FCSTD DOCUMENT  (FreeCAD 0.22R35720 (Git))
Label: polar test v3 
License: All rights reserved
LicenseURL: https://en.wikipedia.org/wiki/All_rights_reserved
objects: TechDraw::DrawViewDimension×8, TechDraw::DrawViewBalloon×7, Sketcher::SketchObject×1, TechDraw::DrawSVGTemplate×1, TechDraw::DrawViewPart×1, TechDraw::DrawPage×1
note: 17 computed .brp shape members not serialized (recipe doc carries the construction recipe); baked Part::Feature solids carry a one-line shape summary decoded from their .brp

FEATURE [Sketcher::SketchObject] Sketch
  FullyConstrained = false
  sketch-geometry (41):
    g0: LineSegment StartX=46.4714 StartY=19.2491 StartZ=0 EndX=19.2491 EndY=46.4714 EndZ=0
    g1: LineSegment StartX=19.2491 StartY=46.4714 StartZ=0 EndX=-19.2491 EndY=46.4714 EndZ=0
    g2: LineSegment StartX=-19.2491 StartY=46.4714 StartZ=0 EndX=-46.4714 EndY=19.2491 EndZ=0
    g3: LineSegment StartX=-46.4714 StartY=19.2491 StartZ=0 EndX=-46.4714 EndY=-19.2491 EndZ=0
    g4: LineSegment StartX=-46.4714 StartY=-19.2491 StartZ=0 EndX=-19.2491 EndY=-46.4714 EndZ=0
    g5: LineSegment StartX=-19.2491 StartY=-46.4714 StartZ=0 EndX=19.2491 EndY=-46.4714 EndZ=0
    g6: LineSegment StartX=19.2491 StartY=-46.4714 StartZ=0 EndX=46.4714 EndY=-19.2491 EndZ=0
    g7: LineSegment StartX=46.4714 StartY=-19.2491 StartZ=0 EndX=46.4714 EndY=19.2491 EndZ=0
    g8: Circle CenterX=0 CenterY=0 CenterZ=0 NormalX=0 NormalY=0 NormalZ=1 AngleXU=0 Radius=50.3003
    g9: LineSegment StartX=79.9038 StartY=0 StartZ=0 EndX=56.5005 EndY=56.5005 EndZ=0
    g10: LineSegment StartX=56.5005 StartY=56.5005 StartZ=0 EndX=0 EndY=79.9038 EndZ=0
    g11: LineSegment StartX=-1.9e-15 StartY=79.9038 StartZ=0 EndX=-56.5005 EndY=56.5005 EndZ=0
    g12: LineSegment StartX=-56.5005 StartY=56.5005 StartZ=0 EndX=-79.9038 EndY=7.1e-15 EndZ=0
    g13: LineSegment StartX=-79.9038 StartY=3.8e-15 StartZ=0 EndX=-56.5005 EndY=-56.5005 EndZ=0
    g14: LineSegment StartX=-56.5005 StartY=-56.5005 StartZ=0 EndX=0 EndY=-79.9038 EndZ=0
    g15: LineSegment StartX=-1.9e-15 StartY=-79.9038 StartZ=0 EndX=56.5005 EndY=-56.5005 EndZ=0
    g16: LineSegment StartX=56.5005 StartY=-56.5005 StartZ=0 EndX=79.9038 EndY=0 EndZ=0
    g17: Circle CenterX=0 CenterY=0 CenterZ=0 NormalX=0 NormalY=0 NormalZ=1 AngleXU=0 Radius=79.9038
    g18: ArcOfCircle CenterX=-19.2491 CenterY=46.4714 CenterZ=0 NormalX=0 NormalY=0 NormalZ=1 AngleXU=0 Radius=8 StartAngle=1.04839 EndAngle=2.8786
    g19: ArcOfCircle CenterX=46.4714 CenterY=-19.2491 CenterZ=0 NormalX=0 NormalY=0 NormalZ=1 AngleXU=0 Radius=8 StartAngle=4.97538 EndAngle=6.80559
    g20: ArcOfCircle CenterX=19.2491 CenterY=-46.4714 CenterZ=0 NormalX=0 NormalY=0 NormalZ=1 AngleXU=0 Radius=8 StartAngle=4.18998 EndAngle=6.02019
    g21: ArcOfCircle CenterX=-19.2491 CenterY=-46.4714 CenterZ=0 NormalX=0 NormalY=0 NormalZ=1 AngleXU=0 Radius=8 StartAngle=3.40458 EndAngle=5.2348
    g22: ArcOfCircle CenterX=-46.4714 CenterY=-19.2491 CenterZ=0 NormalX=0 NormalY=0 NormalZ=1 AngleXU=0 Radius=8 StartAngle=2.61919 EndAngle=4.4494
    g23: ArcOfCircle CenterX=-46.4714 CenterY=19.2491 CenterZ=0 NormalX=0 NormalY=0 NormalZ=1 AngleXU=0 Radius=8 StartAngle=1.83379 EndAngle=3.664
    g24: ArcOfCircle CenterX=-1.9e-15 CenterY=-79.9038 CenterZ=0 NormalX=0 NormalY=0 NormalZ=1 AngleXU=0 Radius=30.5779 StartAngle=1.04839 EndAngle=2.0932
    g25: ArcOfCircle CenterX=-56.5005 CenterY=-56.5005 CenterZ=0 NormalX=0 NormalY=0 NormalZ=1 AngleXU=0 Radius=30.5779 StartAngle=0.262991 EndAngle=1.3078
    g26: ArcOfCircle CenterX=-79.9038 CenterY=3.8e-15 CenterZ=0 NormalX=0 NormalY=0 NormalZ=1 AngleXU=0 Radius=30.5779 StartAngle=5.76078 EndAngle=6.80559
    g27: ArcOfCircle CenterX=-56.5005 CenterY=56.5005 CenterZ=0 NormalX=0 NormalY=0 NormalZ=1 AngleXU=0 Radius=30.5779 StartAngle=4.97538 EndAngle=6.02019
    g28: ArcOfCircle CenterX=-1.9e-15 CenterY=79.9038 CenterZ=0 NormalX=0 NormalY=0 NormalZ=1 AngleXU=0 Radius=30.5779 StartAngle=4.18998 EndAngle=5.2348
    g29: ArcOfCircle CenterX=56.5005 CenterY=-56.5005 CenterZ=0 NormalX=0 NormalY=0 NormalZ=1 AngleXU=0 Radius=30.5779 StartAngle=1.83379 EndAngle=2.8786
    g30: ArcOfCircle CenterX=79.9038 CenterY=3.8e-15 CenterZ=0 NormalX=0 NormalY=0 NormalZ=1 AngleXU=0 Radius=30.5779 StartAngle=2.61919 EndAngle=3.664
    g31: ArcOfCircle CenterX=56.5005 CenterY=56.5005 CenterZ=0 NormalX=0 NormalY=0 NormalZ=1 AngleXU=0 Radius=30.5779 StartAngle=3.40458 EndAngle=4.4494
    g32: ArcOfCircle CenterX=19.2491 CenterY=46.4714 CenterZ=0 NormalX=0 NormalY=0 NormalZ=1 AngleXU=0 Radius=8 StartAngle=0.262991 EndAngle=2.0932
    g33: ArcOfCircle CenterX=46.4714 CenterY=19.2491 CenterZ=0 NormalX=0 NormalY=0 NormalZ=1 AngleXU=0 Radius=8 StartAngle=5.76078 EndAngle=7.59099
    g34: ArcOfCircle CenterX=-79.9038 CenterY=1.276e-13 CenterZ=0 NormalX=0 NormalY=0 NormalZ=1 AngleXU=0 Radius=30.5779 StartAngle=5.76078 EndAngle=6.80559
    g35: ArcOfCircle CenterX=-56.5005 CenterY=-56.5005 CenterZ=0 NormalX=0 NormalY=0 NormalZ=1 AngleXU=0 Radius=30.5779 StartAngle=0.262991 EndAngle=1.30781
    g36: ArcOfCircle CenterX=5.889e-13 CenterY=79.9038 CenterZ=0 NormalX=0 NormalY=0 NormalZ=1 AngleXU=0 Radius=30.5779 StartAngle=4.18998 EndAngle=5.2348
    g37: ArcOfCircle CenterX=-56.5005 CenterY=56.5005 CenterZ=0 NormalX=0 NormalY=0 NormalZ=1 AngleXU=0 Radius=30.5779 StartAngle=4.97538 EndAngle=6.02019
    g38: ArcOfCircle CenterX=-79.9038 CenterY=1.612e-13 CenterZ=0 NormalX=0 NormalY=0 NormalZ=1 AngleXU=0 Radius=30.5779 StartAngle=5.76078 EndAngle=6.80559
    g39: LineSegment StartX=0 StartY=0 StartZ=0 EndX=0 EndY=54.8429 EndZ=0
    g40: LineSegment StartX=0 StartY=0 StartZ=0 EndX=56.3585 EndY=0 EndZ=0
  constraints (85):
    c: Coincident(g0,g1)
    c: Coincident(g1,g2)
    c: Coincident(g2,g3)
    c: Coincident(g3,g4)
    c: Coincident(g4,g5)
    c: Coincident(g5,g6)
    c: Coincident(g6,g7)
    c: Coincident(g7,g0)
    c: Equal(g0, g1-g7) x7
    c: PointOnObject(g0,g8)
    c: PointOnObject(g1,g8)
    c: PointOnObject(g2,g8)
    c: PointOnObject(g3,g8)
    c: PointOnObject(g4,g8)
    c: PointOnObject(g5,g8)
    c: PointOnObject(g6,g8)
    c: PointOnObject(g7,g8)
    c: Coincident(g8,g-1)
    c: Coincident(g9,g10)
    c: Coincident(g10,g11)
    c: Coincident(g11,g12)
    c: Coincident(g12,g13)
    c: Coincident(g13,g14)
    c: Coincident(g14,g15)
    c: Coincident(g15,g16)
    c: Coincident(g16,g9)
    c: Equal(g9, g10-g16) x7
    c: PointOnObject(g9,g17)
    c: PointOnObject(g11,g17)
    c: PointOnObject(g12,g17)
    c: PointOnObject(g13,g17)
    c: PointOnObject(g14,g17)
    c: PointOnObject(g15,g17)
    c: PointOnObject(g16,g17)
    c: Coincident(g17,g8)
    c: PointOnObject(g16,g-1)
    c: Coincident(g18,g1)
    c: Coincident(g19,g6)
    c: Coincident(g20,g5)
    c: Coincident(g21,g4)
    c: Coincident(g22,g3)
    c: Coincident(g23,g2)
    c: Equal(g19,g20)
    c: Equal(g20,g21)
    c: Equal(g21,g22)
    c: Equal(g22,g23)
    c: Coincident(g24,g14)
    c: Coincident(g25,g13)
    c: Coincident(g26,g12)
    c: Coincident(g27,g11)
    c: Coincident(g28,g10)
    c: Equal(g24,g25)
    c: Equal(g25,g26)
    c: Equal(g26,g27)
    c: Radius(g18) = 8
    c: Coincident(g32,g31)
    c: PointOnObject(g32,g28)
    c: Coincident(g33,g31)
    c: Coincident(g33,g30)
    c: Coincident(g19,g30)
    c: Coincident(g19,g29)
    c: Coincident(g23,g27)
    c: Coincident(g23,g26)
    c: PointOnObject(g34,g23)
    c: PointOnObject(g34,g22)
    c: PointOnObject(g35,g22)
    c: Coincident(g22,g26)
    c: Coincident(g22,g25)
    c: Coincident(g21,g25)
    c: Coincident(g21,g24)
    c: Coincident(g20,g24)
    c: Coincident(g20,g29)
    c: Tangent(g18,g28) = 1.5708
    c: Coincident(g18,g27)
    c: PointOnObject(g35,g21)
    c: PointOnObject(g37,g18)
    c: PointOnObject(g36,g18)
    c: PointOnObject(g36,g32)
    c: PointOnObject(g38,g23)
    c: PointOnObject(g37,g23)
    c: PointOnObject(g38,g22)
    c: Coincident(g39,g8)
    c: PointOnObject(g39,g-2)
    c: Coincident(g40,g39)
    c: PointOnObject(g40,g-1)
FEATURE [TechDraw::DrawSVGTemplate] Template
  EditableTexts = Designed_by_Name=Stephen; Drawing_number=T10001; FC-Date=24 Jan 24; FC-SC=NTS; FC-SH=1; FC-Title=Polar Cordinate Test; Subtitle=Test dims for G-Code; Weight=NA
  Height = 210
  Orientation = 1
  Template = F:/Program Files/FreeCAD/data/Mod/TechDraw/Templates/A4_LandscapeTD.svg
  Width = 297
FEATURE [TechDraw::DrawViewPart] View
  CoarseView = false
  Direction = (0,0,1)
  Focus = 100
  HardHidden = false
  IsoCount = 0
  IsoHidden = false
  IsoVisible = false
  LockPosition = false
  Perspective = false
  Rotation = 0
  ScaleType = 0
  ScrubCount = 0
  SeamHidden = false
  SeamVisible = false
  SmoothHidden = false
  SmoothVisible = true
  Source = -> [Sketch]
  X = 82.6714
  XDirection = (1,0,0)
  Y = 102.876
FEATURE [TechDraw::DrawViewDimension] Dimension
  AngleOverride = false
  Arbitrary = false
  ArbitraryTolerances = false
  EqualTolerance = true
  ExtensionAngle = 0
  FormatSpec = C%.3w
  FormatSpecOverTolerance = %+.2w
  FormatSpecUnderTolerance = %+.2w
  Inverted = false
  LineAngle = 0
  LockPosition = false
  MeasureType = 1
  OverTolerance = 0
  References2D = -> [View]
  Rotation = 0
  ScaleType = 0
  TheoreticalExact = false
  Type = 1
  UnderTolerance = 0
  X = 6.68518
  Y = 61.6572
FEATURE [TechDraw::DrawViewDimension] Dimension001
  AngleOverride = false
  Arbitrary = false
  ArbitraryTolerances = false
  EqualTolerance = true
  ExtensionAngle = 0
  FormatSpec = C%.3w
  FormatSpecOverTolerance = %+.2w
  FormatSpecUnderTolerance = %+.2w
  Inverted = false
  LineAngle = 0
  LockPosition = false
  MeasureType = 1
  OverTolerance = 0
  References2D = -> [View]
  Rotation = 0
  ScaleType = 0
  TheoreticalExact = false
  Type = 1
  UnderTolerance = 0
  X = 12.5435
  Y = 68.6572
FEATURE [TechDraw::DrawViewDimension] Dimension002
  AngleOverride = false
  Arbitrary = false
  ArbitraryTolerances = false
  EqualTolerance = true
  ExtensionAngle = 0
  FormatSpec = C%.3w
  FormatSpecOverTolerance = %+.2w
  FormatSpecUnderTolerance = %+.2w
  Inverted = false
  LineAngle = 0
  LockPosition = false
  MeasureType = 1
  OverTolerance = 0
  References2D = -> [View]
  Rotation = 0
  ScaleType = 0
  TheoreticalExact = false
  Type = 1
  UnderTolerance = 0
  X = 23.3321
  Y = 75.6572
FEATURE [TechDraw::DrawViewDimension] Dimension003
  AngleOverride = false
  Arbitrary = false
  ArbitraryTolerances = false
  EqualTolerance = true
  ExtensionAngle = 0
  FormatSpec = C%.3w
  FormatSpecOverTolerance = %+.2w
  FormatSpecUnderTolerance = %+.2w
  Inverted = false
  LineAngle = 0
  LockPosition = false
  MeasureType = 1
  OverTolerance = 0
  References2D = -> [View]
  Rotation = 0
  ScaleType = 0
  TheoreticalExact = false
  Type = 1
  UnderTolerance = 0
  X = 25.7587
  Y = 82.6572
FEATURE [TechDraw::DrawViewDimension] Dimension004
  AngleOverride = false
  Arbitrary = false
  ArbitraryTolerances = false
  EqualTolerance = true
  ExtensionAngle = 0
  FormatSpec = %.3w X30.514
  FormatSpecOverTolerance = %+.2w
  FormatSpecUnderTolerance = %+.2w
  Inverted = false
  LineAngle = 0
  LockPosition = false
  MeasureType = 1
  OverTolerance = 0
  References2D = -> [View]
  Rotation = 0
  ScaleType = 0
  TheoreticalExact = false
  Type = 2
  UnderTolerance = 0
  X = 62.415
  Y = 2.33371
FEATURE [TechDraw::DrawViewDimension] Dimension005
  AngleOverride = false
  Arbitrary = false
  ArbitraryTolerances = false
  EqualTolerance = true
  ExtensionAngle = 0
  FormatSpec = %.3w X53.948
  FormatSpecOverTolerance = %+.2w
  FormatSpecUnderTolerance = %+.2w
  Inverted = false
  LineAngle = 0
  LockPosition = false
  MeasureType = 1
  OverTolerance = 0
  References2D = -> [View]
  Rotation = 0
  ScaleType = 0
  TheoreticalExact = false
  Type = 2
  UnderTolerance = 0
  X = 71.0076
  Y = 2.52937
FEATURE [TechDraw::DrawViewDimension] Dimension006
  AngleOverride = false
  Arbitrary = false
  ArbitraryTolerances = false
  EqualTolerance = true
  ExtensionAngle = 0
  FormatSpec = %.3w X97.102
  FormatSpecOverTolerance = %+.2w
  FormatSpecUnderTolerance = %+.2w
  Inverted = false
  LineAngle = 0
  LockPosition = false
  MeasureType = 1
  OverTolerance = 0
  References2D = -> [View]
  Rotation = 0
  ScaleType = 0
  TheoreticalExact = false
  Type = 2
  UnderTolerance = 0
  X = 78.5385
  Y = 1.81564
FEATURE [TechDraw::DrawViewDimension] Dimension007
  AngleOverride = false
  Arbitrary = false
  ArbitraryTolerances = false
  EqualTolerance = true
  ExtensionAngle = 0
  FormatSpec = %.3w X106.808
  FormatSpecOverTolerance = %+.2w
  FormatSpecUnderTolerance = %+.2w
  Inverted = false
  LineAngle = 0
  LockPosition = false
  MeasureType = 1
  OverTolerance = 0
  References2D = -> [View]
  Rotation = 0
  ScaleType = 0
  TheoreticalExact = false
  Type = 2
  UnderTolerance = 0
  X = 86.0693
  Y = 2.82657
FEATURE [TechDraw::DrawViewBalloon] Balloon001
  BubbleShape = 0
  EndType = 0
  EndTypeScale = 1
  KinkLength = 5
  LockPosition = false
  OriginX = 91.633
  OriginY = -0.0634794
  Rotation = 0
  ScaleType = 0
  ShapeScale = 0.8
  SourceView = -> View
  Text = C
  TextWrapLen = -1
  X = 107.917
  Y = -13.6856
FEATURE [TechDraw::DrawViewBalloon] Balloon002
  BubbleShape = 0
  EndType = 0
  EndTypeScale = 1
  KinkLength = 5
  LockPosition = false
  OriginX = -1.27035
  OriginY = 54.7937
  Rotation = 0
  ScaleType = 0
  ShapeScale = 0.8
  SourceView = -> View
  Text = X
  TextWrapLen = -1
  X = -22.6787
  Y = 64.7071
FEATURE [TechDraw::DrawViewBalloon] Balloon
  BubbleShape = 6
  EndType = 0
  EndTypeScale = 1
  KinkLength = 5
  LockPosition = false
  OriginX = 14.3139
  OriginY = 53.2187
  Rotation = 0
  ScaleType = 0
  ShapeScale = 0.8
  SourceView = -> View
  Text = N502
  TextWrapLen = -1
  X = 6.17742
  Y = 37.8269
FEATURE [TechDraw::DrawViewBalloon] Balloon003
  BubbleShape = 6
  EndType = 0
  EndTypeScale = 1
  KinkLength = 5
  LockPosition = false
  OriginX = 26.8661
  OriginY = 48.9541
  Rotation = 0
  ScaleType = 0
  ShapeScale = 0.8
  SourceView = -> View
  Text = N503
  TextWrapLen = -1
  X = 11.2974
  Y = 28.0766
FEATURE [TechDraw::DrawViewBalloon] Balloon004
  BubbleShape = 6
  EndType = 0
  EndTypeScale = 1
  KinkLength = 5
  LockPosition = false
  OriginX = 47.6077
  OriginY = 26.7883
  Rotation = 0
  ScaleType = 0
  ShapeScale = 0.8
  SourceView = -> View
  Text = N504
  TextWrapLen = -1
  X = 26.9072
  Y = 19.0058
FEATURE [TechDraw::DrawViewBalloon] Balloon005
  BubbleShape = 6
  EndType = 0
  EndTypeScale = 1
  KinkLength = 5
  LockPosition = false
  OriginX = 52.879
  OriginY = 15.3319
  Rotation = 0
  ScaleType = 0
  ShapeScale = 0.8
  SourceView = -> View
  Text = N505
  TextWrapLen = -1
  X = 34.302
  Y = 7.54941
FEATURE [TechDraw::DrawViewBalloon] Balloon006
  BubbleShape = 6
  EndType = 0
  EndTypeScale = 1
  KinkLength = 5
  LockPosition = false
  OriginX = -16.2009
  OriginY = 53.2187
  Rotation = 0
  ScaleType = 0
  ShapeScale = 0.8
  SourceView = -> View
  Text = N501
  TextWrapLen = -1
  X = -12.1272
  Y = 32.1642
FEATURE [TechDraw::DrawPage] Page
  KeepUpdated = true
  NextBalloonIndex = 19
  ProjectionType = 0
  Template = -> Template
  Views = -> [View,Dimension,Dimension001,Dimension002,Dimension003,Dimension004,Dimension005,Dimension006,Dimension007,Balloon001,Balloon002,Balloon,Balloon003,Balloon004,Balloon005,Balloon006]
